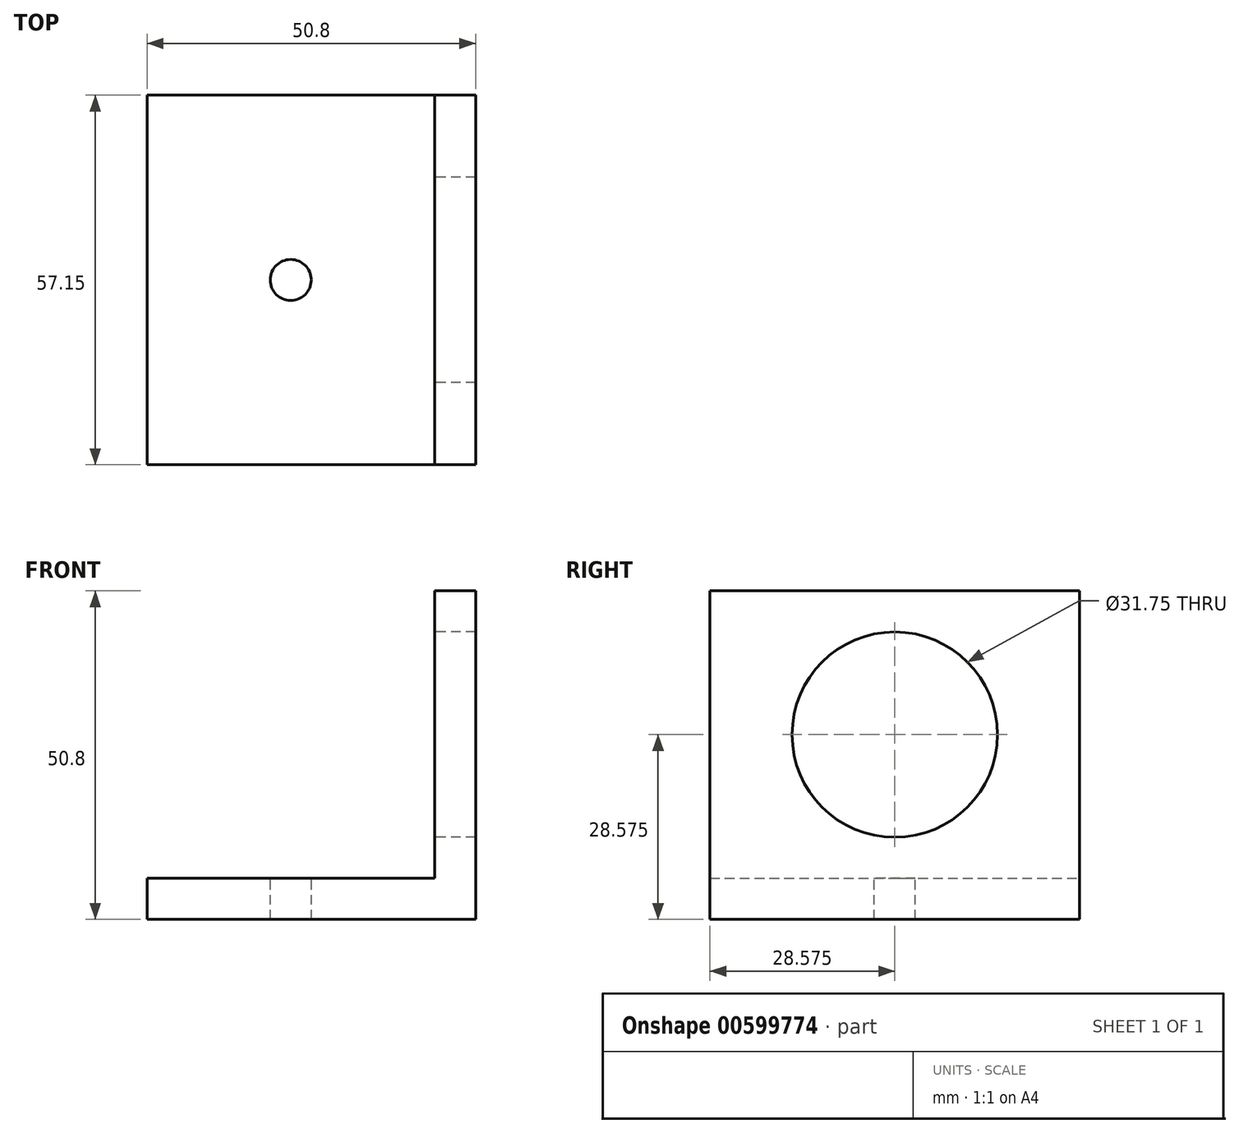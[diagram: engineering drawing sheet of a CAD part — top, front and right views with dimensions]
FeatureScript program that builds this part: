
annotation { "Feature Type Name" : "Feature", "Feature Type Description" : "" }
export const myFeature = defineFeature(function(context is Context, id is Id, definition is map)
    precondition{}
    {
        {
            var Q0;
            Q0=qCreatedBy(makeId("Front.planeOp"),FACE);
            var sketch = newSketch(context, id + "F0", { "sketchPlane" : qUnion([Q0])});
            skLineSegment(sketch, "E0", {"start": v(0, 0) * mm, "end": v(50.8, 0) * mm});
            skLineSegment(sketch, "E1", {"start": v(50.8, 0) * mm, "end": v(50.8, 50.8) * mm});
            skLineSegment(sketch, "E2", {"start": v(50.8, 50.8) * mm, "end": v(44.45, 50.8) * mm});
            skLineSegment(sketch, "E3", {"start": v(44.45, 50.8) * mm, "end": v(44.45, 6.35) * mm});
            skLineSegment(sketch, "E4", {"start": v(44.45, 6.35) * mm, "end": v(0, 6.35) * mm});
            skLineSegment(sketch, "E5", {"start": v(0, 6.35) * mm, "end": v(0, 0) * mm});
            skSolve(sketch);
        }
        {
            var Q0;
            Q0 = qSketchRegion(id + "F0", true);
            extrude(context, id + "F1", {"entities" : qUnion([Q0]), "depth" : 57.15 * mm, "offsetDistance" : 25.4 * mm});
        }
        {
            var Q0;
            Q0=makeQuery(id+"F1.opExtrude","SWEPT_FACE",FACE,{"disambiguationData":[OSD([sQuery(id+"F0.wireOp",EDGE,"E3")])]});
            var sketch = newSketch(context, id + "F2", { "sketchPlane" : qUnion([Q0])});
            skLineSegment(sketch, "E6", {"start": v(0, 28.58) * mm, "end": v(57.15, 28.58) * mm, "construction": true});
            skCircle(sketch, "E7", {"center": v(28.58, 28.57) * mm, "radius": 15.88 * mm});
            skSolve(sketch);
        }
        {
            var Q0;
            Q0=makeQuery(id+"F2.imprint","IMPRINT",FACE,{"disambiguationData":[TD([[makeQuery(id+"F2.imprint","IMPRINT",EDGE,{"derivedFrom":sQuery(id+"F2.wireOp",EDGE,"E7")}),1.0]])]});
            var Q1;
            Q1=sQuery(id+"F2.wireOp",EDGE,"E7");
            extrude(context, id + "F3", {"entities" : qUnion([Q0]), "operationType" : NewBodyOperationType.REMOVE, "surfaceEntities" : qUnion([Q1]), "endBound" : BoundingType.THROUGH_ALL, "oppositeDirection" : true, "depth" : 25.4 * mm, "offsetDistance" : 25.4 * mm});
        }
        {
            var Q0;
            Q0=makeQuery(id+"F1.opExtrude","SWEPT_FACE",FACE,{"disambiguationData":[OSD([sQuery(id+"F0.wireOp",EDGE,"E4")])]});
            var sketch = newSketch(context, id + "F4", { "sketchPlane" : qUnion([Q0])});
            skLineSegment(sketch, "E8", {"start": v(0, 0) * mm, "end": v(44.45, -57.15) * mm, "construction": true});
            skCircle(sketch, "E9", {"center": v(22.23, -28.58) * mm, "radius": 3.18 * mm});
            skSolve(sketch);
        }
        {
            var Q0;
            Q0 = qSketchRegion(id + "F4", true);
            extrude(context, id + "F5", {"entities" : qUnion([Q0]), "operationType" : NewBodyOperationType.REMOVE, "endBound" : BoundingType.THROUGH_ALL, "oppositeDirection" : true, "depth" : 25.4 * mm, "offsetDistance" : 25.4 * mm});
        }
    });
